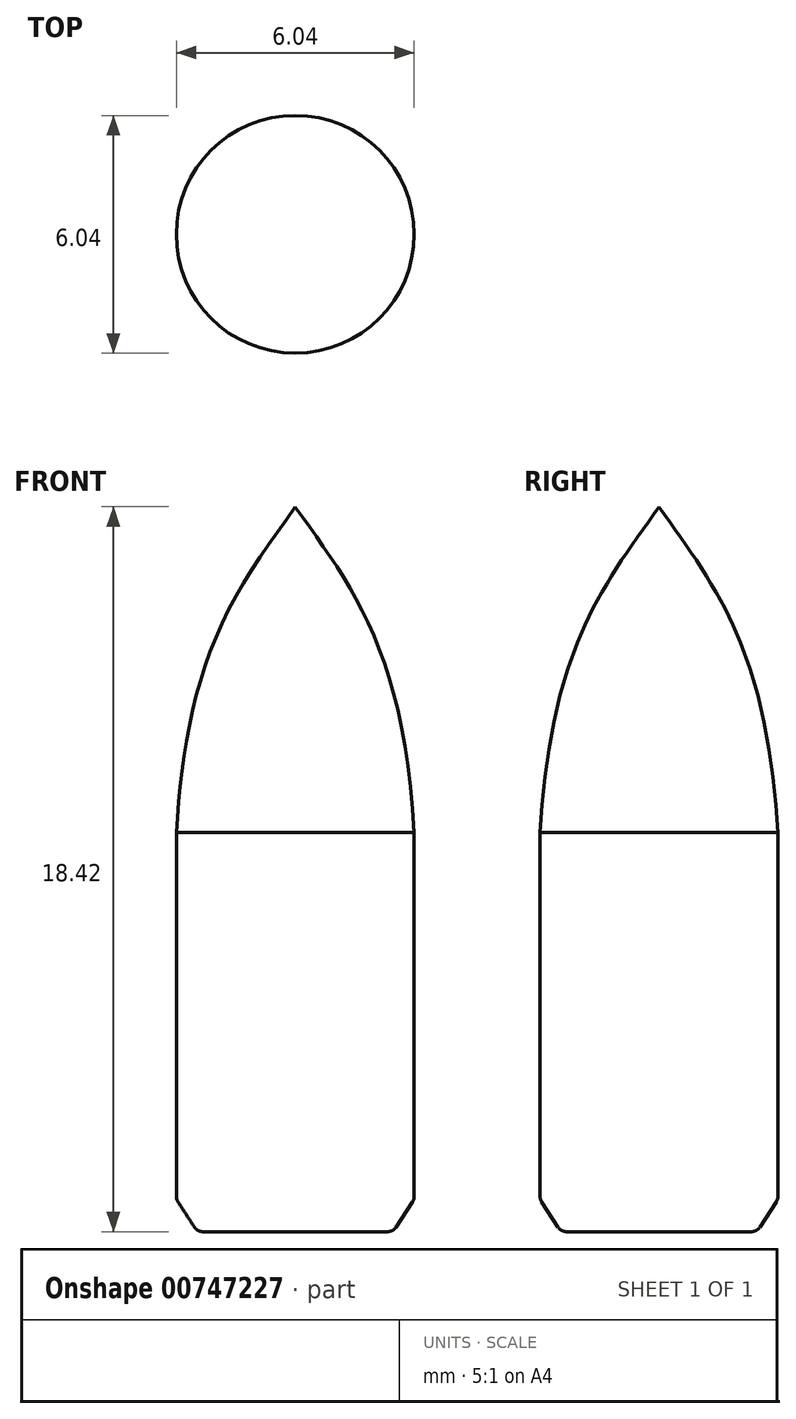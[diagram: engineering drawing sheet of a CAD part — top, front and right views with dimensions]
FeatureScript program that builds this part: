
annotation { "Feature Type Name" : "Feature", "Feature Type Description" : "" }
export const myFeature = defineFeature(function(context is Context, id is Id, definition is map)
    precondition{}
    {
        {
            var Q0;
            Q0=qCreatedBy(makeId("Front.planeOp"),FACE);
            var sketch = newSketch(context, id + "F0", { "sketchPlane" : qUnion([Q0])});
            skLineSegment(sketch, "E0", {"start": v(0, 0) * mm, "end": v(2.35, 0) * mm});
            skLineSegment(sketch, "E1", {"start": v(0, 0) * mm, "end": v(0, 18.41) * mm});
            skLineSegment(sketch, "E2", {"start": v(3.02, 0.9) * mm, "end": v(3.02, 10.14) * mm});
            skFitSpline(sketch, "E3", {"points": [v(0, 18.41) * mm, v(3.02, 10.14) * mm], "startDerivative": vector(4.1, -5.85) * mm, "endDerivative": vector(0.8, -14.13) * mm});
            skLineSegment(sketch, "E4", {"start": v(2.56, 0.12) * mm, "end": v(2.98, 0.76) * mm});
            skArc(sketch, "E5.filletArc", {"start": v(2.98, 0.76) * mm, "mid": v(3, 0.82) * mm, "end": v(3.02, 0.9) * mm});
            skPoint(sketch, "E6.newPointB", {"position": v(2.84, 0) * mm});
            skArc(sketch, "E6.filletArc", {"start": v(2.35, 0) * mm, "mid": v(2.47, 0.03) * mm, "end": v(2.56, 0.12) * mm});
            skSolve(sketch);
        }
        {
            var Q0;
            Q0=qSketchRegion(id+"F0",true);
            var Q1;
            Q1=sQuery(id+"F0.wireOp",EDGE,"E1");
            revolve(context, id + "F1", {"entities" : qUnion([Q0]), "axis" : qUnion([Q1]), "revolveType" : RevolveType.FULL});
        }
    });
